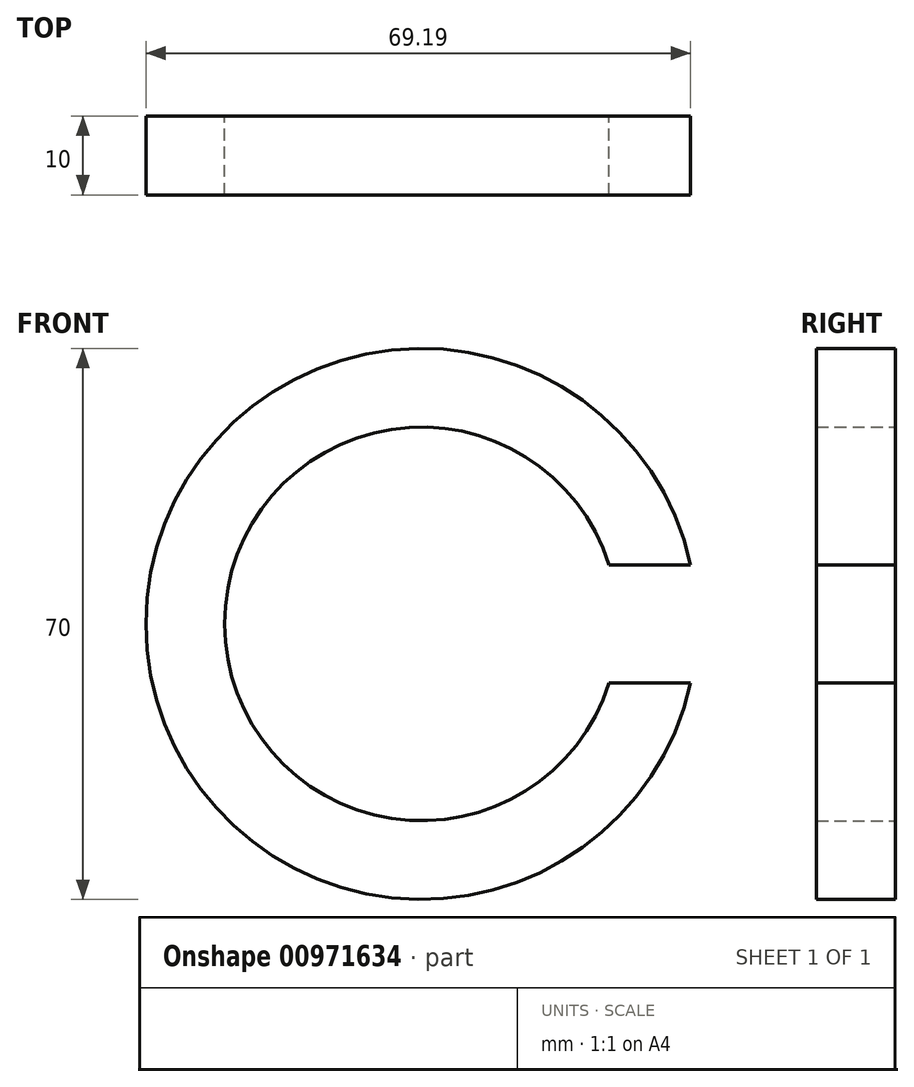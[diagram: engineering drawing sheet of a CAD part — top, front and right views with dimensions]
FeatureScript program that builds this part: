
annotation { "Feature Type Name" : "Feature", "Feature Type Description" : "" }
export const myFeature = defineFeature(function(context is Context, id is Id, definition is map)
    precondition{}
    {
        {
            var Q0;
            Q0=qCreatedBy(makeId("Top.planeOp"),FACE);
            var sketch = newSketch(context, id + "F0", { "sketchPlane" : qUnion([Q0])});
            skLineSegment(sketch, "E0.bottom", {"start": v(-35, 5) * mm, "end": v(-25, 5) * mm});
            skLineSegment(sketch, "E0.top", {"start": v(-35, -5) * mm, "end": v(-25, -5) * mm});
            skLineSegment(sketch, "E0.left", {"start": v(-35, 5) * mm, "end": v(-35, -5) * mm});
            skLineSegment(sketch, "E0.right", {"start": v(-25, 5) * mm, "end": v(-25, -5) * mm});
            skPoint(sketch, "E0.middle", {"position": v(-30, 0) * mm});
            skLineSegment(sketch, "E1", {"start": v(0, 12.15) * mm, "end": v(0, -13.97) * mm});
            skSolve(sketch);
        }
        {
            var Q0;
            Q0 = qSketchRegion(id + "F0", true);
            var Q1;
            Q1=sQuery(id+"F0.wireOp",EDGE,"E1");
            revolve(context, id + "F1", {"surfaceOperationType" : NewSurfaceOperationType.NEW, "entities" : qUnion([Q0]), "axis" : qUnion([Q1]), "revolveType" : RevolveType.FULL});
        }
        {
            var Q0;
            Q0=qCreatedBy(makeId("Top.planeOp"),FACE);
            var sketch = newSketch(context, id + "F2", { "sketchPlane" : qUnion([Q0])});
            skLineSegment(sketch, "E2", {"start": v(23.3, 8) * mm, "end": v(23.3, -9.59) * mm});
            skLineSegment(sketch, "E3", {"start": v(23.3, -9.59) * mm, "end": v(39.92, -9.59) * mm});
            skLineSegment(sketch, "E4", {"start": v(39.92, -9.59) * mm, "end": v(39.92, 8.13) * mm});
            skLineSegment(sketch, "E5", {"start": v(39.92, 8.13) * mm, "end": v(23.3, 8) * mm});
            skSolve(sketch);
        }
        {
            var Q0;
            Q0 = qSketchRegion(id + "F2", true);
            extrude(context, id + "F3", {"entities" : qUnion([Q0]), "operationType" : NewBodyOperationType.REMOVE, "endBound" : BoundingType.SYMMETRIC, "oppositeDirection" : true, "depth" : 15 * mm, "offsetDistance" : 25 * mm});
        }
    });
